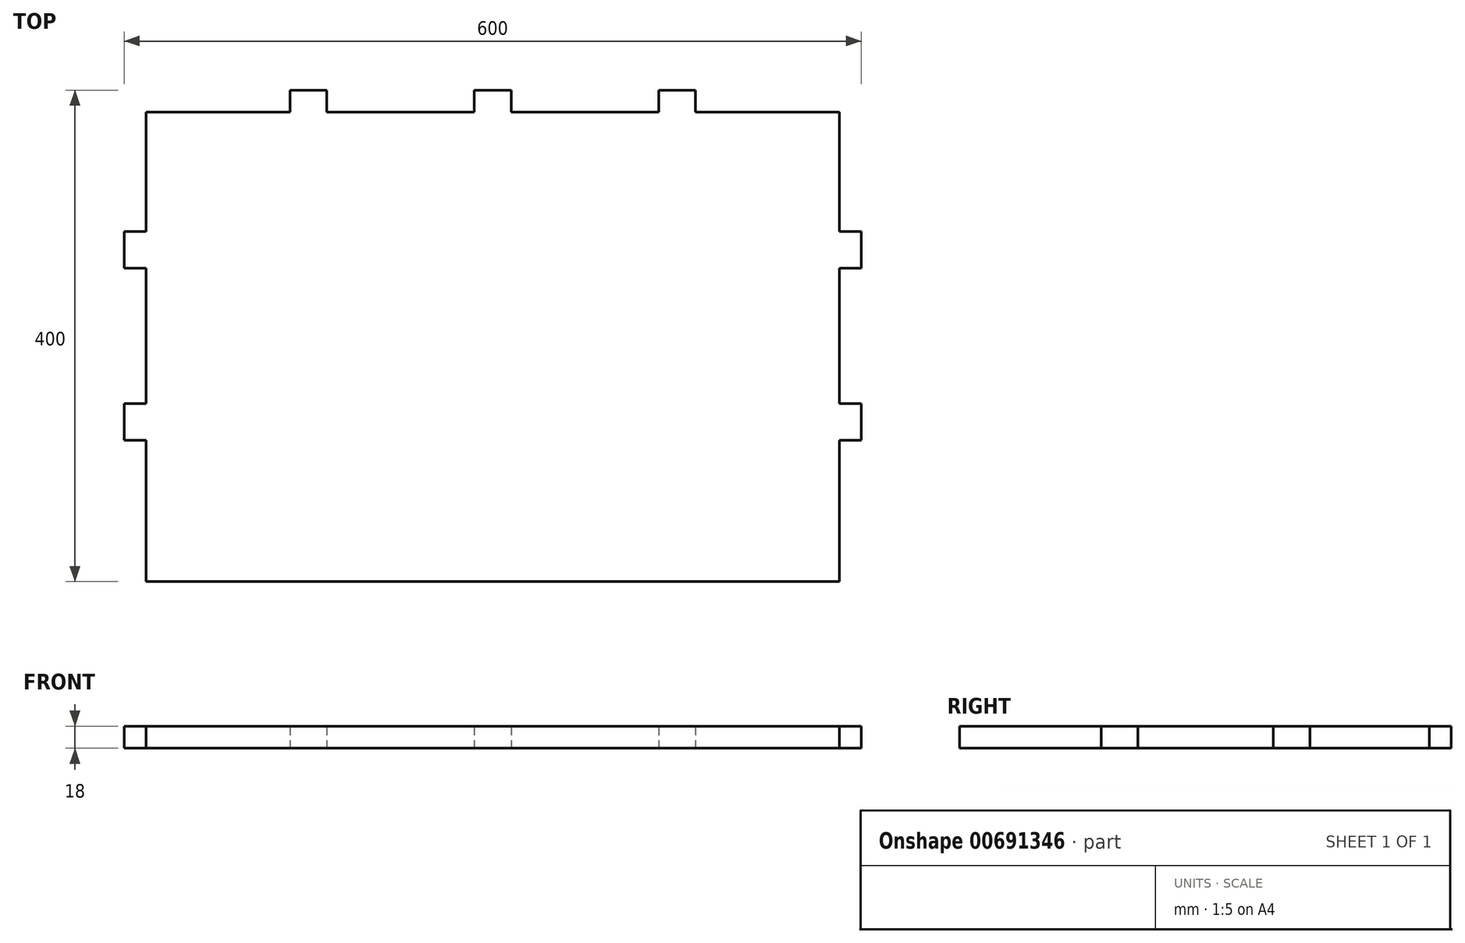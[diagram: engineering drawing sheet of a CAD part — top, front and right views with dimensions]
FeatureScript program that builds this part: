
annotation { "Feature Type Name" : "Feature", "Feature Type Description" : "" }
export const myFeature = defineFeature(function(context is Context, id is Id, definition is map)
    precondition{}
    {
        {
            var Q0;
            Q0=qCreatedBy(makeId("Right.planeOp"),FACE);
            var sketch = newSketch(context, id + "F0", { "sketchPlane" : qUnion([Q0])});
            skLineSegment(sketch, "E0", {"start": v(0, 0) * mm, "end": v(0, 18) * mm});
            skLineSegment(sketch, "E1", {"start": v(0, 18) * mm, "end": v(400, 18) * mm});
            skLineSegment(sketch, "E2", {"start": v(400, 18) * mm, "end": v(400, 0) * mm});
            skLineSegment(sketch, "E3", {"start": v(400, 0) * mm, "end": v(0, 0) * mm});
            skSolve(sketch);
        }
        {
            var Q0;
            Q0=qCreatedBy(makeId("Top.planeOp"),FACE);
            var sketch = newSketch(context, id + "F1", { "sketchPlane" : qUnion([Q0])});
            skLineSegment(sketch, "E4", {"start": v(-300, -47.28) * mm, "end": v(-300, 479.56) * mm, "construction": true});
            skLineSegment(sketch, "E5", {"start": v(-652.6, 200) * mm, "end": v(61.07, 200) * mm, "construction": true});
            skLineSegment(sketch, "E6.MirrorCS", {"start": v(-582, 145) * mm, "end": v(-582, 130) * mm, "construction": true});
            skLineSegment(sketch, "E7.MirrorCS", {"start": v(-582, 115) * mm, "end": v(-582, 130) * mm, "construction": true});
            skLineSegment(sketch, "E8.MirrorCS", {"start": v(0, 270) * mm, "end": v(-18, 270) * mm, "construction": true});
            skLineSegment(sketch, "E9.MirrorCS", {"start": v(-18, 145) * mm, "end": v(-18, 130) * mm, "construction": true});
            skLineSegment(sketch, "E10.MirrorCS", {"start": v(-18, 115) * mm, "end": v(-18, 130) * mm, "construction": true});
            skPoint(sketch, "E11.orphan", {"position": v(0, 200) * mm});
            skPoint(sketch, "E12.orphan", {"position": v(-600, 200) * mm});
            skLineSegment(sketch, "E13", {"start": v(-582, 145) * mm, "end": v(-582, 255) * mm});
            skLineSegment(sketch, "E14", {"start": v(-582, 285) * mm, "end": v(-582, 382) * mm});
            skLineSegment(sketch, "E15", {"start": v(-582, 115) * mm, "end": v(-582, 0) * mm});
            skLineSegment(sketch, "E16", {"start": v(-465, 382) * mm, "end": v(-582, 382) * mm});
            skLineSegment(sketch, "E17", {"start": v(-435, 382) * mm, "end": v(-315, 382) * mm});
            skLineSegment(sketch, "E18", {"start": v(-285, 382) * mm, "end": v(-165, 382) * mm});
            skLineSegment(sketch, "E19", {"start": v(-18, 285) * mm, "end": v(-18, 382) * mm});
            skLineSegment(sketch, "E20", {"start": v(-18, 382) * mm, "end": v(-135, 382) * mm});
            skLineSegment(sketch, "E21", {"start": v(-18, 255) * mm, "end": v(-18, 145) * mm});
            skLineSegment(sketch, "E22", {"start": v(-18, 115) * mm, "end": v(-18, 0) * mm});
            skLineSegment(sketch, "E23", {"start": v(-582, 0) * mm, "end": v(-18, 0) * mm});
            skLineSegment(sketch, "E24", {"start": v(-582, 115) * mm, "end": v(-600, 115) * mm});
            skLineSegment(sketch, "E25", {"start": v(-582, 145) * mm, "end": v(-600, 145) * mm});
            skLineSegment(sketch, "E26", {"start": v(-582, 255) * mm, "end": v(-600, 255) * mm});
            skLineSegment(sketch, "E27", {"start": v(-582, 285) * mm, "end": v(-600, 285) * mm});
            skLineSegment(sketch, "E28", {"start": v(-465, 382) * mm, "end": v(-465, 400) * mm});
            skLineSegment(sketch, "E29", {"start": v(-435, 382) * mm, "end": v(-435, 400) * mm});
            skLineSegment(sketch, "E30", {"start": v(-315, 382) * mm, "end": v(-315, 400) * mm});
            skLineSegment(sketch, "E31", {"start": v(-285, 382) * mm, "end": v(-285, 400) * mm});
            skLineSegment(sketch, "E32", {"start": v(-165, 382) * mm, "end": v(-165, 400) * mm});
            skLineSegment(sketch, "E33", {"start": v(-135, 382) * mm, "end": v(-135, 400) * mm});
            skLineSegment(sketch, "E34", {"start": v(-18, 285) * mm, "end": v(0, 285) * mm});
            skLineSegment(sketch, "E35", {"start": v(-18, 255) * mm, "end": v(0, 255) * mm});
            skLineSegment(sketch, "E36", {"start": v(-18, 145) * mm, "end": v(0, 145) * mm});
            skLineSegment(sketch, "E37", {"start": v(-18, 115) * mm, "end": v(0, 115) * mm});
            skLineSegment(sketch, "E38", {"start": v(-135, 400) * mm, "end": v(-165, 400) * mm});
            skLineSegment(sketch, "E39", {"start": v(-315, 400) * mm, "end": v(-285, 400) * mm});
            skLineSegment(sketch, "E40", {"start": v(-465, 400) * mm, "end": v(-435, 400) * mm});
            skLineSegment(sketch, "E41", {"start": v(-600, 255) * mm, "end": v(-600, 285) * mm});
            skLineSegment(sketch, "E42", {"start": v(-600, 145) * mm, "end": v(-600, 115) * mm});
            skLineSegment(sketch, "E43", {"start": v(0, 145) * mm, "end": v(0, 115) * mm});
            skLineSegment(sketch, "E44", {"start": v(0, 285) * mm, "end": v(0, 255) * mm});
            skPoint(sketch, "E45.3.start.orphan", {"position": v(0, 400) * mm});
            skPoint(sketch, "E45.1.start.orphan", {"position": v(0, 0) * mm});
            skLineSegment(sketch, "E46", {"start": v(-18, 270) * mm, "end": v(-582, 270) * mm, "construction": true});
            skPoint(sketch, "E47.MirrorCS.end.orphan", {"position": v(-582, 270) * mm});
            skPoint(sketch, "E47.MirrorCS.start.orphan", {"position": v(-582, 285) * mm});
            skPoint(sketch, "E48.MirrorCS.start.orphan", {"position": v(-582, 255) * mm});
            skSolve(sketch);
        }
        {
            var Q0;
            Q0=makeQuery(id+"F1.imprint","IMPRINT",FACE,{"disambiguationData":[TD([[makeQuery(id+"F1.imprint","IMPRINT",EDGE,{"derivedFrom":sQuery(id+"F1.wireOp",EDGE,"E13")}),-1.0]])]});
            extrude(context, id + "F2", {"entities" : qUnion([Q0]), "depth" : 18 * mm, "offsetDistance" : 25 * mm});
        }
    });
